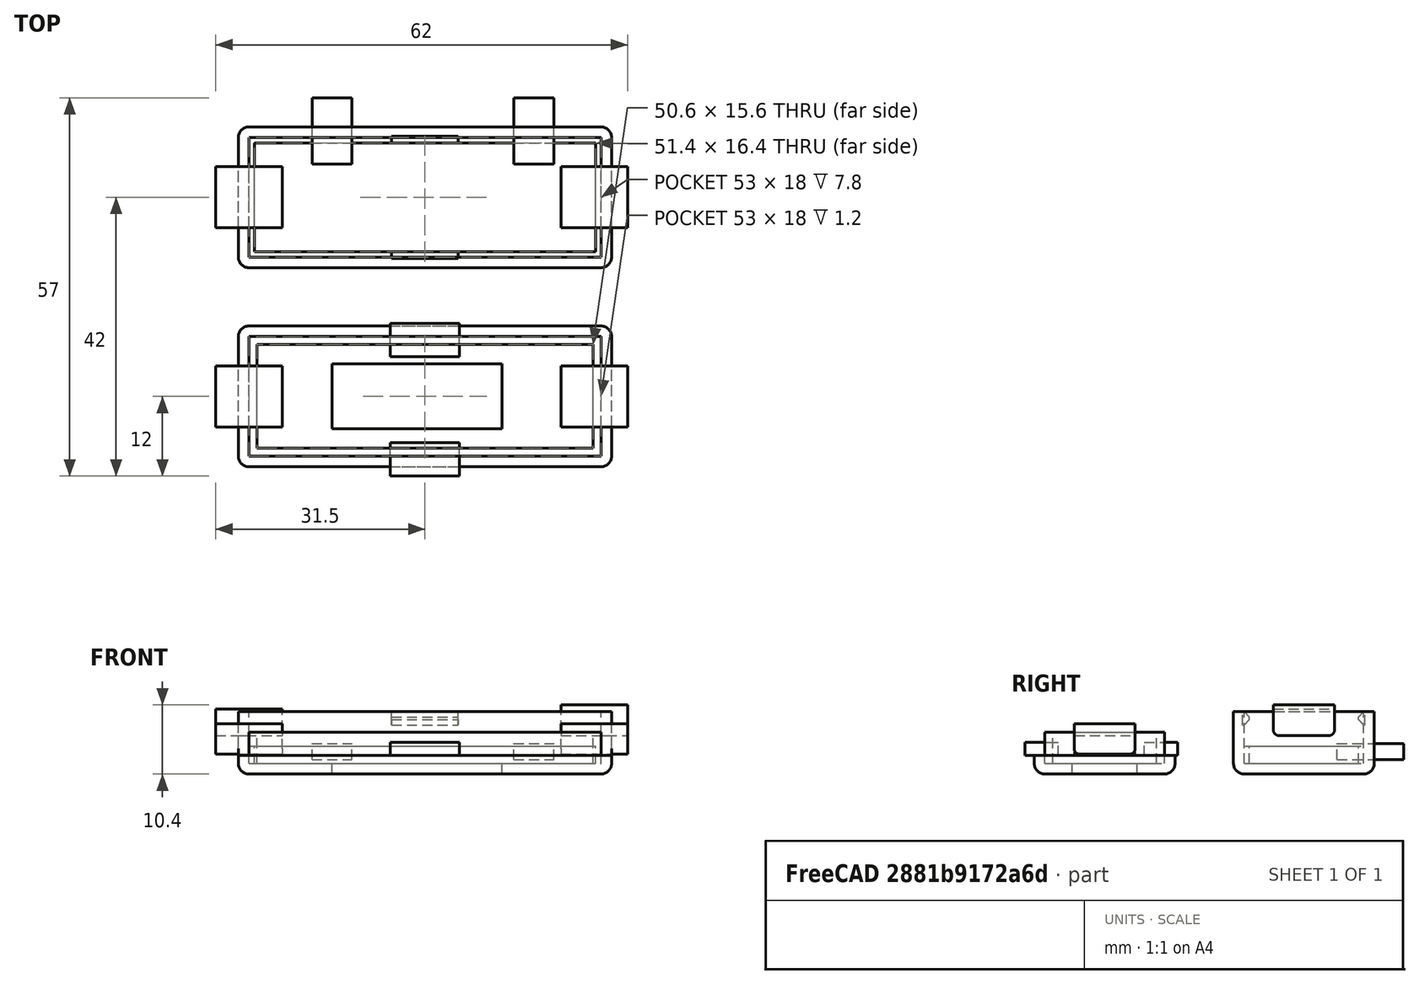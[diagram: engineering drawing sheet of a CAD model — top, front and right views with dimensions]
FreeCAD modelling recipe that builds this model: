
FCSTD DOCUMENT  (FreeCAD 0.16R)
Label: USB-C_Tester_raw_v0.3
License: All rights reserved
LicenseURL: http://en.wikipedia.org/wiki/All_rights_reserved
objects: Part::Box×21, Part::Fillet×6, Part::Cut×4, Part::Chamfer×2
note: 33 computed .brp shape members not serialized (recipe doc carries the construction recipe); baked Part::Feature solids carry a one-line shape summary decoded from their .brp

FEATURE [Part::Box] Box  label="unten_außen"
  Height = 9.4
  Length = 56.2
  Placement = pos=(-1.6,-1.6,0) rot=(0,0,1;0rad)
  Width = 21.2
FEATURE [Part::Box] Box001  label="unten_innen"
  Height = 9.4
  Length = 53
  Placement = pos=(0,0,1.6) rot=(0,0,1;0rad)
  Width = 18
FEATURE [Part::Cut] Cut  label="Schale_roh"
  Base = -> Box
  Tool = -> Box001
FEATURE [Part::Fillet] Fillet  label="Schale_unten"
  Base = -> Cut
  Edges = 8 edges r=1.6: [Edge1,Edge3,Edge4,Edge5,Edge6,Edge14,Edge15,Edge16]
FEATURE [Part::Box] Box002  label="Auflage_außen"
  Height = 2.6
  Length = 53
  Placement = pos=(0,0,1.6) rot=(0,0,1;0rad)
  Width = 18
FEATURE [Part::Box] Box003  label="Auflage_innen"
  Height = 2.6
  Length = 51.4
  Placement = pos=(0.8,0.8,1.6) rot=(0,0,1;0rad)
  Width = 16.4
FEATURE [Part::Cut] Cut001  label="Auflage"
  Base = -> Box002
  Tool = -> Box003
FEATURE [Part::Box] Box004  label="Haken1_roh"
  Height = 2
  Length = 10
  Placement = pos=(21.5,-0.2,7.4) rot=(0,0,1;0rad)
  Width = 1
FEATURE [Part::Chamfer] Chamfer  label="Haken1"
  Base = -> Box004
  Edges = 2 edges r=0.8: [Edge11,Edge12]
FEATURE [Part::Box] Box005  label="Haken2_roh"
  Height = 2
  Length = 10
  Placement = pos=(21.5,17.2,7.4) rot=(0,0,1;0rad)
  Width = 1
FEATURE [Part::Chamfer] Chamfer001  label="Haken2"
  Base = -> Box005
  Edges = 2 edges r=0.8: [Edge9,Edge10]
FEATURE [Part::Box] Box006  label="USB_Buchse1_roh"
  Height = 4
  Length = 10
  Placement = pos=(-5,4.4,5.8) rot=(0,0,1;0rad)
  Width = 9.2
FEATURE [Part::Box] Box008  label="Button1"
  Height = 2.4
  Length = 6
  Placement = pos=(9.5,14,2.2) rot=(0,0,1;0rad)
  Width = 10
FEATURE [Part::Box] Box009  label="Button2"
  Height = 2.4
  Length = 6
  Placement = pos=(39.9,14,2.2) rot=(0,0,1;0rad)
  Width = 10
FEATURE [Part::Box] Box010  label="oben_außen"
  Height = 2.8
  Length = 56.2
  Placement = pos=(-1.6,-31.6,0) rot=(0,0,1;0rad)
  Width = 21.2
FEATURE [Part::Box] Box011  label="oben_innen"
  Height = 9.4
  Length = 53
  Placement = pos=(0,-30,1.6) rot=(0,0,1;0rad)
  Width = 18
FEATURE [Part::Cut] Cut002  label="Schale_oben_roh"
  Base = -> Box010
  Tool = -> Box011
FEATURE [Part::Fillet] Fillet001  label="Schale_oben"
  Base = -> Cut002
  Edges = 8 edges r=1.6: [Edge1,Edge3,Edge4,Edge5,Edge6,Edge14,Edge15,Edge16]
FEATURE [Part::Box] Box012  label="Rahmen_außen"
  Height = 4.7
  Length = 53
  Placement = pos=(0,-30,1.6) rot=(0,0,1;0rad)
  Width = 18
FEATURE [Part::Box] Box013  label="Rahmen_innen"
  Height = 4.8
  Length = 50.6
  Placement = pos=(1.2,-28.8,1.6) rot=(0,0,1;0rad)
  Width = 15.6
FEATURE [Part::Cut] Cut003  label="Rahmen"
  Base = -> Box012
  Tool = -> Box013
FEATURE [Part::Box] Box014  label="OLED"
  Height = 1.6
  Length = 25.6
  Placement = pos=(12.5,-25.9,0) rot=(0,0,1;0rad)
  Width = 9.8
FEATURE [Part::Box] Box017  label="Oese1"
  Height = 2
  Length = 10.4
  Placement = pos=(21.3,-33,2.8) rot=(0,0,1;0rad)
  Width = 5
FEATURE [Part::Box] Box018  label="Oese2"
  Height = 2
  Length = 10.4
  Placement = pos=(21.3,-15,2.8) rot=(0,0,1;0rad)
  Width = 5
FEATURE [Part::Box] Box019  label="USB_Buchse2_roh"
  Height = 4.6
  Length = 10
  Placement = pos=(47,4.4,5.8) rot=(0,0,1;0rad)
  Width = 9.2
FEATURE [Part::Box] Box020  label="USB_Buchse3_roh"
  Height = 4.6
  Length = 10
  Placement = pos=(-5,-25.6,3) rot=(0,0,1;0rad)
  Width = 9.2
FEATURE [Part::Box] Box021  label="USB_Buchse4_roh"
  Height = 4.6
  Length = 10
  Placement = pos=(47,-25.6,3) rot=(0,0,1;0rad)
  Width = 9.2
FEATURE [Part::Fillet] Fillet002  label="USB_Buchse1"
  Base = -> Box006
  Edges = 2 edges r=0.8: [Edge9,Edge11]
FEATURE [Part::Fillet] Fillet003  label="USB_Buchse2"
  Base = -> Box019
  Edges = 2 edges r=0.8: [Edge9,Edge11]
FEATURE [Part::Box] Box022  label="Nut1"
  Height = 3
  Length = 1.6
  Placement = pos=(-1.6,-25.5,2.8) rot=(0,0,1;0rad)
  Width = 9
FEATURE [Part::Box] Box023  label="Nut2"
  Height = 3
  Length = 1.6
  Placement = pos=(53,-25.5,2.8) rot=(0,0,1;0rad)
  Width = 9
FEATURE [Part::Fillet] Fillet004  label="USB-Buchse3"
  Base = -> Box020
  Edges = 2 edges r=0.8: [Edge9,Edge11]
FEATURE [Part::Fillet] Fillet005  label="USB-Buchse4"
  Base = -> Box021
  Edges = 2 edges r=0.8: [Edge9,Edge11]
